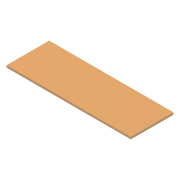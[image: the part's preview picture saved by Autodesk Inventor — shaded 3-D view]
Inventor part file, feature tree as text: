
AUTODESK INVENTOR PART (.ipt)
format: ipt  version: 2014 (Build 180170000, 170)  size: 79,360 bytes
history: native  units: mm
features: extrude x1, sketch x1
ambient origin geometry x8: Origin, YZ Plane, XZ Plane, XY Plane, X Axis, Y Axis, Z Axis, Center Point
bodies: Solid1 (feature_tree)
feature tree (2):
  extrude  "Extrusion1"  Depth=175.0mm
  sketch  "Sketch1"  dims[d0=60.0mm d1=175.0mm d2=3.0mm d3=0.0mm]
